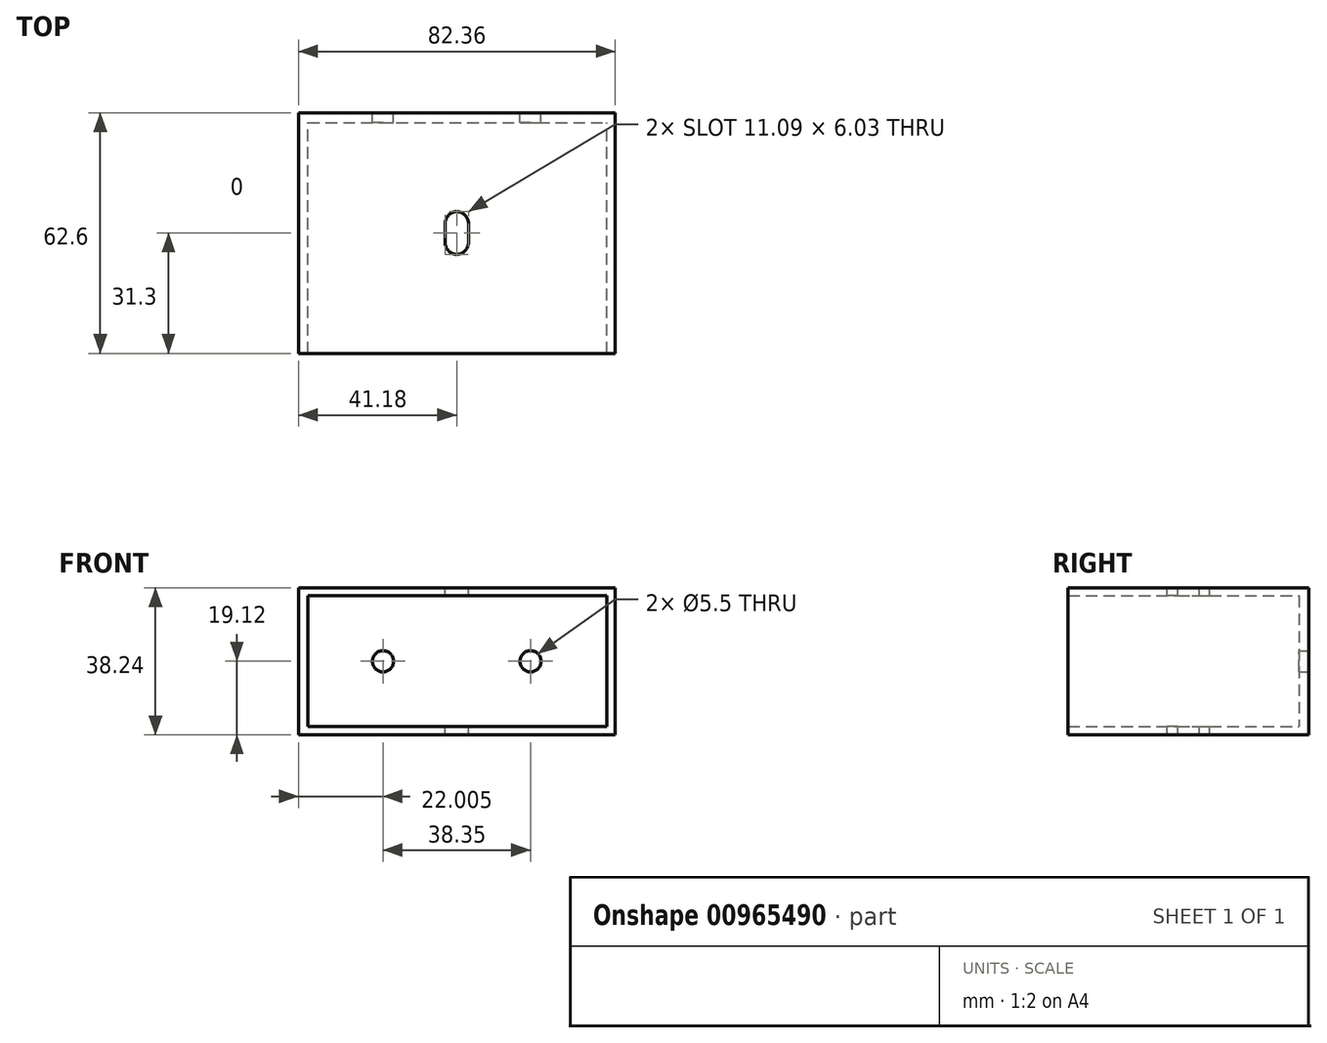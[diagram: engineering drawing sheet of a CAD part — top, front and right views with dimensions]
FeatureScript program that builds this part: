
annotation { "Feature Type Name" : "Feature", "Feature Type Description" : "" }
export const myFeature = defineFeature(function(context is Context, id is Id, definition is map)
    precondition{}
    {
        {
            var Q0;
            Q0=qCreatedBy(makeId("Front.planeOp"),FACE);
            var sketch = newSketch(context, id + "F0", { "sketchPlane" : qUnion([Q0])});
            skLineSegment(sketch, "E0.bottom", {"start": v(41.17, 19.12) * mm, "end": v(-41.17, 19.12) * mm});
            skLineSegment(sketch, "E0.top", {"start": v(41.17, -19.13) * mm, "end": v(-41.17, -19.13) * mm});
            skLineSegment(sketch, "E0.left", {"start": v(41.17, 19.12) * mm, "end": v(41.17, -19.13) * mm});
            skLineSegment(sketch, "E0.right", {"start": v(-41.17, 19.12) * mm, "end": v(-41.17, -19.13) * mm});
            skPoint(sketch, "E0.middle", {"position": v(0, 0) * mm});
            skSolve(sketch);
        }
        {
            var Q0;
            Q0 = qSketchRegion(id + "F0", true);
            extrude(context, id + "F1", {"entities" : qUnion([Q0]), "depth" : 2.6 * mm, "offsetDistance" : 25 * mm});
        }
        {
            var Q0;
            Q0=makeQuery(id+"F1.opExtrude","CAP_FACE",FACE,{"disambiguationData":[OSD([sQuery(id+"F0.wireOp",EDGE,"E0.bottom"),sQuery(id+"F0.wireOp",EDGE,"E0.top"),sQuery(id+"F0.wireOp",EDGE,"E0.left"),sQuery(id+"F0.wireOp",EDGE,"E0.right")])],"isStart":false});
            var sketch = newSketch(context, id + "F2", { "sketchPlane" : qUnion([Q0])});
            skLineSegment(sketch, "E1", {"start": v(-41.17, 19.12) * mm, "end": v(-41.17, 15.4) * mm});
            skLineSegment(sketch, "E2", {"start": v(-38.67, 19.12) * mm, "end": v(-38.67, 17.02) * mm, "construction": true});
            skLineSegment(sketch, "E3", {"start": v(41.17, 17.02) * mm, "end": v(39.07, 17.02) * mm, "construction": true});
            skLineSegment(sketch, "E4", {"start": v(-38.67, 17.02) * mm, "end": v(39.07, 17.02) * mm});
            skLineSegment(sketch, "E5", {"start": v(39.07, 17.02) * mm, "end": v(39.07, 0) * mm});
            skPoint(sketch, "E5.endSnap0", {"position": v(41.17, 0) * mm});
            skLineSegment(sketch, "E6", {"start": v(-38.67, 17.02) * mm, "end": v(-38.67, 15.4) * mm});
            skPoint(sketch, "E7.visualSharp", {"position": v(-38.67, 15.05) * mm});
            skPoint(sketch, "E8.visualSharp", {"position": v(-41.17, 15.05) * mm});
            skLineSegment(sketch, "E9", {"start": v(39.07, 0) * mm, "end": v(0, 0) * mm, "construction": true});
            skLineSegment(sketch, "E10.MirrorCS", {"start": v(-38.67, -17.02) * mm, "end": v(-38.67, -15.4) * mm});
            skLineSegment(sketch, "E11.MirrorCS", {"start": v(-38.67, -19.12) * mm, "end": v(-38.67, -17.02) * mm, "construction": true});
            skLineSegment(sketch, "E12.MirrorCS", {"start": v(41.17, -17.02) * mm, "end": v(39.07, -17.02) * mm, "construction": true});
            skLineSegment(sketch, "E13.MirrorCS", {"start": v(39.07, -17.02) * mm, "end": v(39.07, 0) * mm});
            skPoint(sketch, "E14.MirrorP", {"position": v(-38.67, -15.05) * mm});
            skLineSegment(sketch, "E15.MirrorCS", {"start": v(-38.67, -17.02) * mm, "end": v(39.07, -17.02) * mm});
            skPoint(sketch, "E16.MirrorP", {"position": v(-41.17, -15.05) * mm});
            skLineSegment(sketch, "E17.MirrorCS", {"start": v(-41.17, -19.12) * mm, "end": v(-41.17, -15.4) * mm});
            skLineSegment(sketch, "E18", {"start": v(-41.17, 19.12) * mm, "end": v(41.17, 19.12) * mm});
            skLineSegment(sketch, "E19", {"start": v(41.17, 19.12) * mm, "end": v(41.17, -19.13) * mm});
            skLineSegment(sketch, "E20", {"start": v(41.17, -19.13) * mm, "end": v(-41.17, -19.12) * mm});
            skLineSegment(sketch, "E21", {"start": v(-41.17, 15.4) * mm, "end": v(-41.17, 15.05) * mm});
            skLineSegment(sketch, "E22", {"start": v(-38.67, 15.4) * mm, "end": v(-38.67, 15.05) * mm});
            skLineSegment(sketch, "E23", {"start": v(-38.67, -15.4) * mm, "end": v(-38.67, -15.05) * mm});
            skLineSegment(sketch, "E24", {"start": v(-41.17, -15.05) * mm, "end": v(-41.17, -15.4) * mm});
            skPoint(sketch, "E7.filletArc.end.orphan", {"position": v(-38.67, 15.4) * mm});
            skLineSegment(sketch, "E25", {"start": v(-41.17, 15.05) * mm, "end": v(-41.17, -15.05) * mm});
            skLineSegment(sketch, "E26", {"start": v(-38.67, -15.05) * mm, "end": v(-38.67, 15.05) * mm});
            skSolve(sketch);
        }
        {
            var Q0;
            Q0 = qSketchRegion(id + "F2", true);
            extrude(context, id + "F3", {"entities" : qUnion([Q0]), "operationType" : NewBodyOperationType.ADD, "depth" : 60 * mm, "offsetDistance" : 25 * mm});
        }
        {
            var Q0;
            Q0=makeQuery(id+"F1.opExtrude","CAP_FACE",FACE,{"disambiguationData":[OSD([sQuery(id+"F0.wireOp",EDGE,"E0.bottom"),sQuery(id+"F0.wireOp",EDGE,"E0.top"),sQuery(id+"F0.wireOp",EDGE,"E0.left"),sQuery(id+"F0.wireOp",EDGE,"E0.right")])],"isStart":true});
            var sketch = newSketch(context, id + "F4", { "sketchPlane" : qUnion([Q0])});
            skLineSegment(sketch, "E27", {"start": v(41.17, 0) * mm, "end": v(19.17, 0) * mm, "construction": true});
            skCircle(sketch, "E28", {"center": v(19.17, 0) * mm, "radius": 2.75 * mm});
            skLineSegment(sketch, "E29", {"start": v(19.17, 0) * mm, "end": v(-19.18, 0) * mm, "construction": true});
            skCircle(sketch, "E30", {"center": v(-19.18, 0) * mm, "radius": 2.75 * mm});
            skSolve(sketch);
        }
        {
            var Q0;
            Q0 = qSketchRegion(id + "F4", true);
            extrude(context, id + "F5", {"entities" : qUnion([Q0]), "operationType" : NewBodyOperationType.REMOVE, "oppositeDirection" : true, "depth" : 25 * mm, "offsetDistance" : 25 * mm});
        }
        {
            var Q0;
            Q0=makeQuery(id+"F3.boolean.opBoolean","MERGE",FACE,{"derivedFrom":[makeQuery(id+"F1.opExtrude","SWEPT_FACE",FACE,{"disambiguationData":[OSD([sQuery(id+"F0.wireOp",EDGE,"E0.bottom")])]}),makeQuery(id+"F3.opExtrude","SWEPT_FACE",FACE,{"disambiguationData":[OSD([sQuery(id+"F2.wireOp",EDGE,"E18")])]})]});
            var sketch = newSketch(context, id + "F6", { "sketchPlane" : qUnion([Q0])});
            skLineSegment(sketch, "E31", {"start": v(-41.18, -62.6) * mm, "end": v(41.18, 0) * mm, "construction": true});
            skLineSegment(sketch, "E32", {"start": v(0, -31.3) * mm, "end": v(-5.55, -31.3) * mm, "construction": true});
            skLineSegment(sketch, "E33", {"start": v(0, -31.3) * mm, "end": v(0, -34.31) * mm, "construction": true});
            skLineSegment(sketch, "E34", {"start": v(3.01, -31.3) * mm, "end": v(3.01, -34.07) * mm});
            skLineSegment(sketch, "E35.MirrorCS", {"start": v(3.01, -31.3) * mm, "end": v(3.01, -28.53) * mm});
            skLineSegment(sketch, "E36.MirrorCS", {"start": v(-3.01, -31.3) * mm, "end": v(-3.01, -28.53) * mm});
            skLineSegment(sketch, "E37.MirrorCS", {"start": v(-3.01, -31.3) * mm, "end": v(-3.01, -34.07) * mm});
            skPoint(sketch, "E38.visualSharp", {"position": v(-5.55, -28.29) * mm});
            skArc(sketch, "E39", {"start": v(-3.01, -34.07) * mm, "mid": v(0, -36.85) * mm, "end": v(3.01, -34.07) * mm});
            skPoint(sketch, "E39.startSnap0", {"position": v(-2.77, -34.31) * mm});
            skPoint(sketch, "E40.orphan", {"position": v(-5.55, -34.31) * mm});
            skArc(sketch, "E41.MirrorCS", {"start": v(-3.01, -28.53) * mm, "mid": v(0, -25.75) * mm, "end": v(3.01, -28.53) * mm});
            skPoint(sketch, "E42.orphan", {"position": v(5.55, -34.31) * mm});
            skPoint(sketch, "E43.orphan", {"position": v(5.55, -28.29) * mm});
            skSolve(sketch);
        }
        {
            var Q0;
            Q0 = qSketchRegion(id + "F6", true);
            extrude(context, id + "F7", {"entities" : qUnion([Q0]), "operationType" : NewBodyOperationType.REMOVE, "endBound" : BoundingType.THROUGH_ALL, "oppositeDirection" : true, "depth" : 25 * mm, "offsetDistance" : 25 * mm});
        }
    });
